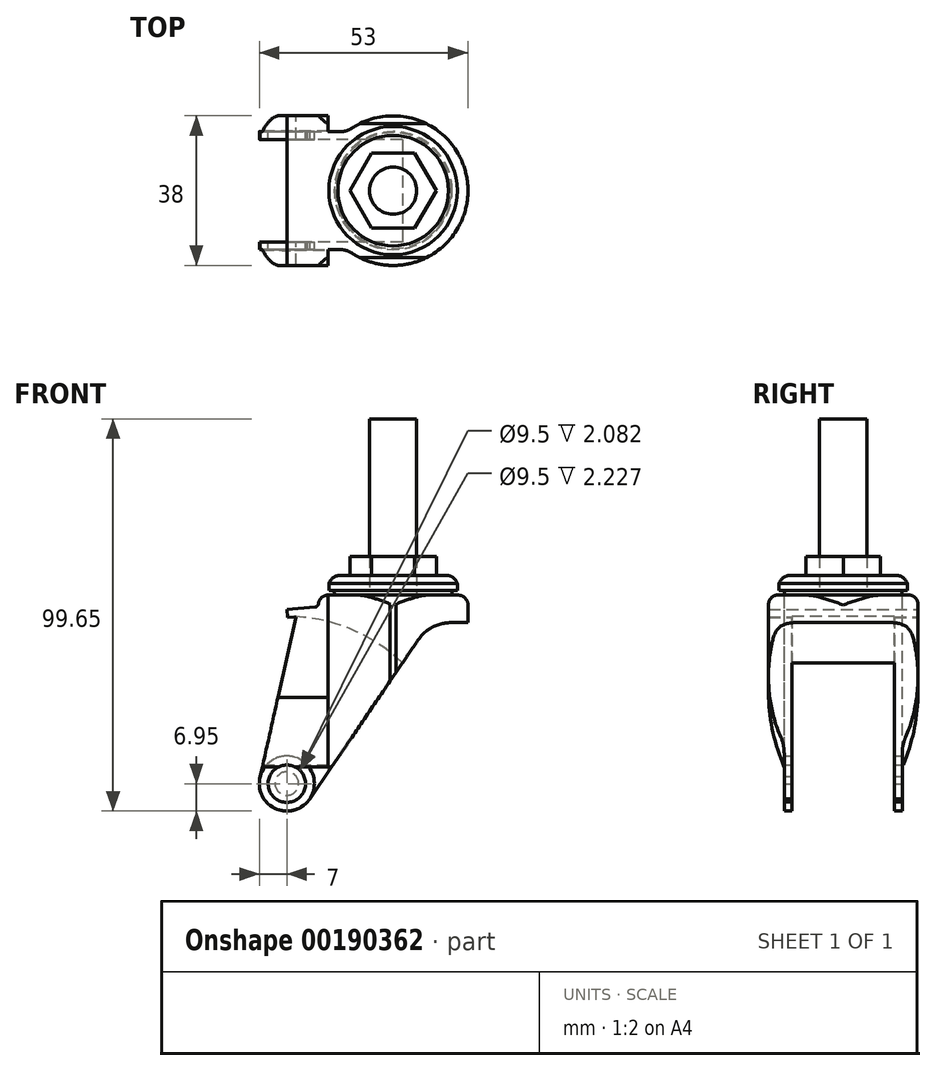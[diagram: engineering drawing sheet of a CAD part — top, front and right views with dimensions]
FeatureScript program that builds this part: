
annotation { "Feature Type Name" : "Feature", "Feature Type Description" : "" }
export const myFeature = defineFeature(function(context is Context, id is Id, definition is map)
    precondition{}
    {
        {
            var Q0;
            Q0=qCreatedBy(makeId("Top.planeOp"),FACE);
            var sketch = newSketch(context, id + "F0", { "sketchPlane" : qUnion([Q0])});
            skCircle(sketch, "E0", {"center": v(0, 0) * mm, "radius": 16.3 * mm});
            skArc(sketch, "E1", {"start": v(-10.5, -15.83) * mm, "mid": v(19, 0) * mm, "end": v(-10.5, 15.83) * mm});
            skLineSegment(sketch, "E2", {"start": v(22, 0) * mm, "end": v(-67.5, 0) * mm});
            skLineSegment(sketch, "E3", {"start": v(-31.35, 12.5) * mm, "end": v(-25.1, 12.5) * mm});
            skLineSegment(sketch, "E4", {"start": v(-25.25, 12) * mm, "end": v(-35, 12) * mm});
            skLineSegment(sketch, "E5", {"start": v(-31.35, -12.5) * mm, "end": v(-25.1, -12.5) * mm});
            skLineSegment(sketch, "E6", {"start": v(-25.25, -12) * mm, "end": v(-35, -12) * mm});
            skLineSegment(sketch, "E7", {"start": v(-25.67, -10.5) * mm, "end": v(-64.5, -10.5) * mm});
            skLineSegment(sketch, "E8", {"start": v(-25.67, 10.5) * mm, "end": v(-64.5, 10.5) * mm});
            skLineSegment(sketch, "E9", {"start": v(-30.25, -17.5) * mm, "end": v(-23.75, -17.5) * mm});
            skLineSegment(sketch, "E10", {"start": v(-29.75, 16.5) * mm, "end": v(-24.25, 16.5) * mm});
            skLineSegment(sketch, "E11", {"start": v(-24.94, 13) * mm, "end": v(-33.5, 13) * mm});
            skLineSegment(sketch, "E12", {"start": v(-13.27, 15) * mm, "end": v(-33.5, 15) * mm});
            skLineSegment(sketch, "E13", {"start": v(-24.94, -13) * mm, "end": v(-33.5, -13) * mm});
            skLineSegment(sketch, "E14", {"start": v(-13.27, -15) * mm, "end": v(-33.5, -15) * mm});
            skLineSegment(sketch, "E15", {"start": v(-30, -13) * mm, "end": v(-30, -12.5) * mm});
            skArc(sketch, "E16", {"start": v(-32.19, -12) * mm, "mid": v(-31.84, -12.37) * mm, "end": v(-31.35, -12.5) * mm});
            skLineSegment(sketch, "E17", {"start": v(-31.75, -16) * mm, "end": v(-31.75, -15.2) * mm});
            skArc(sketch, "E18", {"start": v(-31.55, -15) * mm, "mid": v(-31.7, -15.06) * mm, "end": v(-31.75, -15.2) * mm});
            skArc(sketch, "E19", {"start": v(-31.75, -16) * mm, "mid": v(-31.31, -17.06) * mm, "end": v(-30.25, -17.5) * mm});
            skLineSegment(sketch, "E20", {"start": v(-33.5, -13) * mm, "end": v(-33.5, -15) * mm});
            skLineSegment(sketch, "E21", {"start": v(-33.5, 15) * mm, "end": v(-33.5, 13) * mm});
            skArc(sketch, "E22", {"start": v(-31.35, 12.5) * mm, "mid": v(-31.84, 12.37) * mm, "end": v(-32.19, 12) * mm});
            skLineSegment(sketch, "E23", {"start": v(-30, 13) * mm, "end": v(-30, 12.5) * mm});
            skArc(sketch, "E24", {"start": v(-29.75, 16.5) * mm, "mid": v(-30.81, 16.06) * mm, "end": v(-31.25, 15) * mm});
            skLineSegment(sketch, "E25", {"start": v(-27, 19.5) * mm, "end": v(-27, -20.5) * mm});
            skLineSegment(sketch, "E26", {"start": v(5.48, -9.5) * mm, "end": v(10.97, 0) * mm});
            skLineSegment(sketch, "E27", {"start": v(-10.97, 0) * mm, "end": v(-5.48, -9.5) * mm});
            skCircle(sketch, "E28", {"center": v(0, 0) * mm, "radius": 6 * mm});
            skCircle(sketch, "E29", {"center": v(0, 0) * mm, "radius": 5.05 * mm});
            skCircle(sketch, "E30", {"center": v(0, 0) * mm, "radius": 4 * mm});
            skArc(sketch, "E31", {"start": v(-24.23, 15) * mm, "mid": v(-27, 0) * mm, "end": v(-24.23, -15) * mm});
            skArc(sketch, "E32", {"start": v(-13.86, 13) * mm, "mid": v(-19, 0) * mm, "end": v(-13.86, -13) * mm});
            skLineSegment(sketch, "E33", {"start": v(0, -22) * mm, "end": v(0, 22) * mm});
            skLineSegment(sketch, "E34", {"start": v(-22.25, -16) * mm, "end": v(-22.25, -15.2) * mm});
            skArc(sketch, "E35", {"start": v(-22.25, -15.2) * mm, "mid": v(-22.3, -15.06) * mm, "end": v(-22.45, -15) * mm});
            skArc(sketch, "E36", {"start": v(-23.75, -17.5) * mm, "mid": v(-22.69, -17.06) * mm, "end": v(-22.25, -16) * mm});
            skArc(sketch, "E37", {"start": v(-10.5, -15.83) * mm, "mid": v(-11.82, -15.21) * mm, "end": v(-13.27, -15) * mm});
            skLineSegment(sketch, "E38", {"start": v(-5.48, -9.5) * mm, "end": v(5.48, -9.5) * mm});
            skLineSegment(sketch, "E39", {"start": v(-5.48, 9.5) * mm, "end": v(-10.97, 0) * mm});
            skArc(sketch, "E40", {"start": v(-22.75, 15) * mm, "mid": v(-23.19, 16.06) * mm, "end": v(-24.25, 16.5) * mm});
            skArc(sketch, "E41", {"start": v(-13.27, 15) * mm, "mid": v(-11.82, 15.21) * mm, "end": v(-10.5, 15.83) * mm});
            skLineSegment(sketch, "E42", {"start": v(5.48, 9.5) * mm, "end": v(-5.48, 9.5) * mm});
            skLineSegment(sketch, "E43", {"start": v(10.97, 0) * mm, "end": v(5.48, 9.5) * mm});
            skLineSegment(sketch, "E44", {"start": v(-64.5, 10.5) * mm, "end": v(-64.5, -10.5) * mm});
            skLineSegment(sketch, "E45", {"start": v(-35, -12) * mm, "end": v(-35, -10.5) * mm});
            skLineSegment(sketch, "E46", {"start": v(-35, 10.5) * mm, "end": v(-35, 12) * mm});
            skSolve(sketch);
        }
        {
            var Q0;
            Q0=qCreatedBy(makeId("Front.planeOp"),FACE);
            var sketch = newSketch(context, id + "F1", { "sketchPlane" : qUnion([Q0])});
            skArc(sketch, "E47", {"start": v(10.72, -7.97) * mm, "mid": v(11.8, -7.76) * mm, "end": v(12.75, -7.18) * mm});
            skLineSegment(sketch, "E48", {"start": v(-67.5, -47.93) * mm, "end": v(13.5, -47.93) * mm});
            skArc(sketch, "E49", {"start": v(14.63, -7) * mm, "mid": v(9.95, -8.16) * mm, "end": v(6.36, -11.37) * mm});
            skLineSegment(sketch, "E50", {"start": v(-12.46, -6.65) * mm, "end": v(-12.46, -34.22) * mm});
            skLineSegment(sketch, "E51", {"start": v(-24.23, -3.46) * mm, "end": v(-33.83, -46.4) * mm});
            skLineSegment(sketch, "E52", {"start": v(0, 47.77) * mm, "end": v(0, -26.76) * mm});
            skArc(sketch, "E53", {"start": v(-25.8, -10.45) * mm, "mid": v(-41.9, -82.34) * mm, "end": v(-0.48, -21.42) * mm});
            skLineSegment(sketch, "E54", {"start": v(-27, -88.43) * mm, "end": v(-27, -40.18) * mm});
            skArc(sketch, "E55", {"start": v(-33.8, -46.3) * mm, "mid": v(-29.83, -54.33) * mm, "end": v(-21.21, -51.87) * mm});
            skCircle(sketch, "E56", {"center": v(-27, -47.93) * mm, "radius": 4.75 * mm});
            skLineSegment(sketch, "E57", {"start": v(6.36, -11.37) * mm, "end": v(-21.21, -51.87) * mm});
            skLineSegment(sketch, "E58", {"start": v(6, 10.37) * mm, "end": v(6, 42.77) * mm});
            skLineSegment(sketch, "E59", {"start": v(5.05, 12.01) * mm, "end": v(5.05, 43.72) * mm});
            skLineSegment(sketch, "E60", {"start": v(-6, 10.37) * mm, "end": v(-6, 42.77) * mm});
            skLineSegment(sketch, "E61", {"start": v(-5.05, 12.01) * mm, "end": v(-5.05, 43.72) * mm});
            skLineSegment(sketch, "E62", {"start": v(-14.05, 4.97) * mm, "end": v(14.05, 4.97) * mm});
            skLineSegment(sketch, "E63", {"start": v(16.3, 2.97) * mm, "end": v(-16.3, 2.97) * mm});
            skLineSegment(sketch, "E64", {"start": v(10.97, 9.77) * mm, "end": v(-10.97, 9.77) * mm});
            skLineSegment(sketch, "E65", {"start": v(16.3, 1.17) * mm, "end": v(-16.3, 1.17) * mm});
            skLineSegment(sketch, "E66", {"start": v(-16.51, 0) * mm, "end": v(16.5, 0) * mm});
            skLineSegment(sketch, "E67", {"start": v(-10.97, 9.77) * mm, "end": v(-10.97, 5.32) * mm});
            skLineSegment(sketch, "E68", {"start": v(-13.37, -2.5) * mm, "end": v(-27, -3.7) * mm});
            skArc(sketch, "E69", {"start": v(-16.5, 0) * mm, "mid": v(-18.16, -0.63) * mm, "end": v(-18.98, -2.2) * mm});
            skLineSegment(sketch, "E70", {"start": v(-27, -3.7) * mm, "end": v(-26.83, -5.7) * mm});
            skLineSegment(sketch, "E71", {"start": v(-24.69, -5.5) * mm, "end": v(-26.83, -5.7) * mm});
            skArc(sketch, "E72", {"start": v(-19.89, -3.08) * mm, "mid": v(-19.28, -2.8) * mm, "end": v(-18.98, -2.2) * mm});
            skArc(sketch, "E73", {"start": v(-10.9, 5.27) * mm, "mid": v(-10.6, 5.11) * mm, "end": v(-10.3, 4.97) * mm});
            skLineSegment(sketch, "E74", {"start": v(-10.37, 4.97) * mm, "end": v(-10.97, 5.32) * mm});
            skArc(sketch, "E75", {"start": v(-14.05, 4.97) * mm, "mid": v(-15.44, 4.27) * mm, "end": v(-16.3, 2.97) * mm});
            skArc(sketch, "E76", {"start": v(-14.98, 1.17) * mm, "mid": v(-14.94, 0.57) * mm, "end": v(-14.72, 0) * mm});
            skLineSegment(sketch, "E77", {"start": v(-13, 2.57) * mm, "end": v(-13, -1.5) * mm});
            skLineSegment(sketch, "E78", {"start": v(-16.3, 2.97) * mm, "end": v(-16.3, 1.17) * mm});
            skLineSegment(sketch, "E79", {"start": v(10.97, 9.77) * mm, "end": v(10.97, 5.32) * mm});
            skLineSegment(sketch, "E80", {"start": v(-5.48, 9.77) * mm, "end": v(-5.48, 5.32) * mm});
            skLineSegment(sketch, "E81", {"start": v(10.72, -7.97) * mm, "end": v(10.33, -7.97) * mm});
            skArc(sketch, "E82", {"start": v(-5.48, 5.32) * mm, "mid": v(-4.86, 5.13) * mm, "end": v(-4.23, 4.97) * mm});
            skArc(sketch, "E83", {"start": v(-6, 4.97) * mm, "mid": v(-5.73, 5.13) * mm, "end": v(-5.48, 5.32) * mm});
            skLineSegment(sketch, "E84", {"start": v(-6, 12.01) * mm, "end": v(6, 12.01) * mm});
            skArc(sketch, "E85", {"start": v(-6.6, 9.77) * mm, "mid": v(-6.18, 9.95) * mm, "end": v(-6, 10.37) * mm});
            skLineSegment(sketch, "E86", {"start": v(-5.05, 12.01) * mm, "end": v(-6, 10.37) * mm});
            skLineSegment(sketch, "E87", {"start": v(5.05, 12.01) * mm, "end": v(6, 10.37) * mm});
            skArc(sketch, "E88", {"start": v(6, 10.37) * mm, "mid": v(6.18, 9.95) * mm, "end": v(6.6, 9.77) * mm});
            skLineSegment(sketch, "E89", {"start": v(4, 44.77) * mm, "end": v(-4, 44.77) * mm});
            skLineSegment(sketch, "E90", {"start": v(6, 42.77) * mm, "end": v(-6, 42.77) * mm});
            skLineSegment(sketch, "E91", {"start": v(-4, 44.77) * mm, "end": v(-6, 42.77) * mm});
            skLineSegment(sketch, "E92", {"start": v(6, 42.77) * mm, "end": v(4, 44.77) * mm});
            skLineSegment(sketch, "E93", {"start": v(19, -2.5) * mm, "end": v(19, -6) * mm});
            skLineSegment(sketch, "E94", {"start": v(19, -2.9) * mm, "end": v(19, -7) * mm});
            skLineSegment(sketch, "E95", {"start": v(14.63, -7) * mm, "end": v(19, -7) * mm});
            skArc(sketch, "E96", {"start": v(16.3, 2.97) * mm, "mid": v(15.44, 4.27) * mm, "end": v(14.05, 4.97) * mm});
            skLineSegment(sketch, "E97", {"start": v(16.3, 2.97) * mm, "end": v(16.3, 1.17) * mm});
            skArc(sketch, "E98", {"start": v(19, -2.5) * mm, "mid": v(18.27, -0.73) * mm, "end": v(16.5, 0) * mm});
            skLineSegment(sketch, "E99", {"start": v(10.37, 4.97) * mm, "end": v(10.97, 5.32) * mm});
            skArc(sketch, "E100", {"start": v(10.3, 4.97) * mm, "mid": v(10.6, 5.11) * mm, "end": v(10.9, 5.27) * mm});
            skArc(sketch, "E101", {"start": v(5.48, 5.32) * mm, "mid": v(5.73, 5.13) * mm, "end": v(6, 4.97) * mm});
            skArc(sketch, "E102", {"start": v(4.23, 4.97) * mm, "mid": v(4.86, 5.13) * mm, "end": v(5.48, 5.32) * mm});
            skLineSegment(sketch, "E103", {"start": v(13, 2.57) * mm, "end": v(13, -1.5) * mm});
            skArc(sketch, "E104", {"start": v(14.72, 0) * mm, "mid": v(14.94, 0.57) * mm, "end": v(14.98, 1.17) * mm});
            skLineSegment(sketch, "E105", {"start": v(5.48, 9.77) * mm, "end": v(5.48, 5.32) * mm});
            skSolve(sketch);
        }
        {
            var Q0;
            Q0=qCreatedBy(makeId("Right.planeOp"),FACE);
            var sketch = newSketch(context, id + "F2", { "sketchPlane" : qUnion([Q0])});
            skLineSegment(sketch, "E106", {"start": v(13.01, -54.88) * mm, "end": v(13.01, -6.64) * mm});
            skLineSegment(sketch, "E107", {"start": v(15.01, -54.88) * mm, "end": v(15.01, -6.65) * mm});
            skLineSegment(sketch, "E108", {"start": v(19.01, -25.96) * mm, "end": v(19.01, -2.45) * mm});
            skLineSegment(sketch, "E109", {"start": v(-18.99, -25.96) * mm, "end": v(-18.99, -2.45) * mm});
            skLineSegment(sketch, "E110", {"start": v(-14.99, -54.88) * mm, "end": v(-14.99, -6.65) * mm});
            skLineSegment(sketch, "E111", {"start": v(-12.99, -54.88) * mm, "end": v(-12.99, -6.64) * mm});
            skLineSegment(sketch, "E112", {"start": v(0.01, 47.77) * mm, "end": v(0.01, -88.38) * mm});
            skArc(sketch, "E113", {"start": v(-18.99, -25.96) * mm, "mid": v(-17.81, -34.98) * mm, "end": v(-15.04, -43.63) * mm});
            skLineSegment(sketch, "E114", {"start": v(20.26, -47.88) * mm, "end": v(-19.24, -47.88) * mm});
            skLineSegment(sketch, "E115", {"start": v(12.01, -55.88) * mm, "end": v(12.01, -39.88) * mm});
            skLineSegment(sketch, "E116", {"start": v(10.51, -85.38) * mm, "end": v(10.51, -10.38) * mm});
            skLineSegment(sketch, "E117", {"start": v(-11.99, -55.88) * mm, "end": v(-11.99, -39.88) * mm});
            skLineSegment(sketch, "E118", {"start": v(-10.49, -85.38) * mm, "end": v(-10.49, -10.38) * mm});
            skArc(sketch, "E119", {"start": v(15.28, -43.13) * mm, "mid": v(17.9, -34.71) * mm, "end": v(19.01, -25.96) * mm});
            skLineSegment(sketch, "E120", {"start": v(-12.99, -44.88) * mm, "end": v(-11.99, -44.88) * mm});
            skLineSegment(sketch, "E121", {"start": v(-14.99, -54.88) * mm, "end": v(-12.99, -54.88) * mm});
            skArc(sketch, "E122", {"start": v(-14.99, -43.63) * mm, "mid": v(-16.05, -44.07) * mm, "end": v(-16.49, -45.13) * mm});
            skArc(sketch, "E123", {"start": v(-16.49, -50.63) * mm, "mid": v(-16.05, -51.7) * mm, "end": v(-14.99, -52.13) * mm});
            skLineSegment(sketch, "E124", {"start": v(-16.49, -50.63) * mm, "end": v(-16.49, -45.13) * mm});
            skLineSegment(sketch, "E125", {"start": v(13.01, -44.88) * mm, "end": v(12.01, -44.88) * mm});
            skLineSegment(sketch, "E126", {"start": v(13.01, -54.88) * mm, "end": v(15.01, -54.88) * mm});
            skArc(sketch, "E127", {"start": v(17.51, -44.63) * mm, "mid": v(17.08, -43.57) * mm, "end": v(16.01, -43.13) * mm});
            skArc(sketch, "E128", {"start": v(15.22, -43.13) * mm, "mid": v(15.08, -43.19) * mm, "end": v(15.01, -43.33) * mm});
            skLineSegment(sketch, "E129", {"start": v(16.01, -43.13) * mm, "end": v(15.21, -43.13) * mm});
            skArc(sketch, "E130", {"start": v(16.01, -52.63) * mm, "mid": v(17.08, -52.2) * mm, "end": v(17.51, -51.13) * mm});
            skArc(sketch, "E131", {"start": v(15.01, -52.43) * mm, "mid": v(15.08, -52.57) * mm, "end": v(15.22, -52.63) * mm});
            skLineSegment(sketch, "E132", {"start": v(16.01, -52.63) * mm, "end": v(15.21, -52.63) * mm});
            skLineSegment(sketch, "E133", {"start": v(17.51, -51.13) * mm, "end": v(17.51, -44.63) * mm});
            skArc(sketch, "E134", {"start": v(-16.49, 0.05) * mm, "mid": v(-18.25, -0.68) * mm, "end": v(-18.99, -2.45) * mm});
            skLineSegment(sketch, "E135", {"start": v(5.07, 12.01) * mm, "end": v(5.07, 43.72) * mm});
            skLineSegment(sketch, "E136", {"start": v(6.01, 10.37) * mm, "end": v(6.01, 42.77) * mm});
            skLineSegment(sketch, "E137", {"start": v(-5.04, 12.01) * mm, "end": v(-5.04, 43.72) * mm});
            skLineSegment(sketch, "E138", {"start": v(-5.99, 10.37) * mm, "end": v(-5.99, 42.77) * mm});
            skLineSegment(sketch, "E139", {"start": v(10.73, -7.92) * mm, "end": v(-10.7, -7.92) * mm});
            skLineSegment(sketch, "E140", {"start": v(-14.04, 4.97) * mm, "end": v(14.06, 4.97) * mm});
            skLineSegment(sketch, "E141", {"start": v(9.51, 5.32) * mm, "end": v(-9.49, 5.32) * mm});
            skLineSegment(sketch, "E142", {"start": v(-9.49, 9.77) * mm, "end": v(9.51, 9.77) * mm});
            skLineSegment(sketch, "E143", {"start": v(-5.99, 12.01) * mm, "end": v(6.01, 12.01) * mm});
            skLineSegment(sketch, "E144", {"start": v(16.31, 1.17) * mm, "end": v(-16.29, 1.17) * mm});
            skLineSegment(sketch, "E145", {"start": v(16.31, 2.97) * mm, "end": v(-16.29, 2.97) * mm});
            skLineSegment(sketch, "E146", {"start": v(-11.99, -5.64) * mm, "end": v(12.01, -5.64) * mm});
            skLineSegment(sketch, "E147", {"start": v(-11.99, -3.65) * mm, "end": v(12.01, -3.65) * mm});
            skLineSegment(sketch, "E148", {"start": v(-16.5, 0.05) * mm, "end": v(16.51, 0.05) * mm});
            skLineSegment(sketch, "E149", {"start": v(0.01, 9.77) * mm, "end": v(0.01, 5.32) * mm});
            skLineSegment(sketch, "E150", {"start": v(-9.49, 5.32) * mm, "end": v(-9.49, 9.77) * mm});
            skLineSegment(sketch, "E151", {"start": v(-8.88, 4.97) * mm, "end": v(-9.49, 5.32) * mm});
            skArc(sketch, "E152", {"start": v(-9.49, 5.32) * mm, "mid": v(-8.95, 5.14) * mm, "end": v(-8.4, 4.97) * mm});
            skArc(sketch, "E153", {"start": v(-12.99, -6.87) * mm, "mid": v(-11.96, -7.64) * mm, "end": v(-10.7, -7.92) * mm});
            skArc(sketch, "E154", {"start": v(-14.04, 4.97) * mm, "mid": v(-15.43, 4.28) * mm, "end": v(-16.29, 2.97) * mm});
            skLineSegment(sketch, "E155", {"start": v(-12.99, 2.62) * mm, "end": v(-12.99, -1.45) * mm});
            skArc(sketch, "E156", {"start": v(-14.96, 1.17) * mm, "mid": v(-14.93, 0.57) * mm, "end": v(-14.7, 0) * mm});
            skLineSegment(sketch, "E157", {"start": v(-16.29, 2.97) * mm, "end": v(-16.29, 1.17) * mm});
            skArc(sketch, "E158", {"start": v(-11.99, -3.65) * mm, "mid": v(-14.1, -4.52) * mm, "end": v(-14.99, -6.65) * mm});
            skArc(sketch, "E159", {"start": v(-11.99, -5.64) * mm, "mid": v(-12.7, -5.93) * mm, "end": v(-12.99, -6.64) * mm});
            skArc(sketch, "E160", {"start": v(0.01, 5.32) * mm, "mid": v(0.55, 5.14) * mm, "end": v(1.1, 4.97) * mm});
            skArc(sketch, "E161", {"start": v(-1.07, 4.97) * mm, "mid": v(-0.52, 5.14) * mm, "end": v(0.01, 5.32) * mm});
            skLineSegment(sketch, "E162", {"start": v(-5.04, 12.01) * mm, "end": v(-5.99, 10.37) * mm});
            skArc(sketch, "E163", {"start": v(-6.59, 9.77) * mm, "mid": v(-6.16, 9.95) * mm, "end": v(-5.99, 10.37) * mm});
            skLineSegment(sketch, "E164", {"start": v(9.51, 5.32) * mm, "end": v(9.51, 9.77) * mm});
            skArc(sketch, "E165", {"start": v(10.73, -7.92) * mm, "mid": v(11.99, -7.64) * mm, "end": v(13.01, -6.87) * mm});
            skLineSegment(sketch, "E166", {"start": v(8.91, 4.97) * mm, "end": v(9.51, 5.32) * mm});
            skArc(sketch, "E167", {"start": v(8.43, 4.97) * mm, "mid": v(8.98, 5.14) * mm, "end": v(9.51, 5.32) * mm});
            skLineSegment(sketch, "E168", {"start": v(16.31, 2.97) * mm, "end": v(16.31, 1.17) * mm});
            skLineSegment(sketch, "E169", {"start": v(13.01, 2.62) * mm, "end": v(13.01, -1.45) * mm});
            skArc(sketch, "E170", {"start": v(14.74, 0) * mm, "mid": v(14.95, 0.57) * mm, "end": v(15, 1.17) * mm});
            skArc(sketch, "E171", {"start": v(16.31, 2.97) * mm, "mid": v(15.46, 4.28) * mm, "end": v(14.06, 4.97) * mm});
            skArc(sketch, "E172", {"start": v(19.01, -2.45) * mm, "mid": v(18.28, -0.68) * mm, "end": v(16.51, 0.05) * mm});
            skArc(sketch, "E173", {"start": v(13.01, -6.64) * mm, "mid": v(12.72, -5.93) * mm, "end": v(12.01, -5.64) * mm});
            skArc(sketch, "E174", {"start": v(15.01, -6.65) * mm, "mid": v(14.14, -4.52) * mm, "end": v(12.01, -3.65) * mm});
            skLineSegment(sketch, "E175", {"start": v(5.07, 12.01) * mm, "end": v(6.01, 10.37) * mm});
            skArc(sketch, "E176", {"start": v(6.01, 10.37) * mm, "mid": v(6.2, 9.95) * mm, "end": v(6.61, 9.77) * mm});
            skLineSegment(sketch, "E177", {"start": v(4.01, 44.77) * mm, "end": v(-3.99, 44.77) * mm});
            skLineSegment(sketch, "E178", {"start": v(6.01, 42.77) * mm, "end": v(-5.99, 42.77) * mm});
            skLineSegment(sketch, "E179", {"start": v(-3.99, 44.77) * mm, "end": v(-5.99, 42.77) * mm});
            skLineSegment(sketch, "E180", {"start": v(6.01, 42.77) * mm, "end": v(4.01, 44.77) * mm});
            skLineSegment(sketch, "E181", {"start": v(12.01, -39.88) * mm, "end": v(10.51, -39.88) * mm});
            skLineSegment(sketch, "E182", {"start": v(-10.49, -10.38) * mm, "end": v(10.51, -10.38) * mm});
            skLineSegment(sketch, "E183", {"start": v(-10.49, -39.88) * mm, "end": v(-11.99, -39.88) * mm});
            skLineSegment(sketch, "E184", {"start": v(-10.49, -85.38) * mm, "end": v(10.51, -85.38) * mm});
            skLineSegment(sketch, "E185", {"start": v(-10.49, -55.88) * mm, "end": v(-11.99, -55.88) * mm});
            skLineSegment(sketch, "E186", {"start": v(12.01, -55.88) * mm, "end": v(10.51, -55.88) * mm});
            skLineSegment(sketch, "E187", {"start": v(-12.99, -50.88) * mm, "end": v(-11.99, -50.88) * mm});
            skLineSegment(sketch, "E188", {"start": v(13.01, -50.88) * mm, "end": v(12.01, -50.88) * mm});
            skSolve(sketch);
        }
        {
            var Q0;
            Q0=qCreatedBy(makeId("Front.planeOp"),FACE);
            var sketch = newSketch(context, id + "F3", { "sketchPlane" : qUnion([Q0])});
            skLineSegment(sketch, "E189", {"start": v(0, 60.42) * mm, "end": v(0, -88.2) * mm, "construction": true});
            skLineSegment(sketch, "E190", {"start": v(-75.21, 0) * mm, "end": v(74.5, 0) * mm, "construction": true});
            skLineSegment(sketch, "E191.0", {"start": v(-67.5, -47.93) * mm, "end": v(13.5, -47.93) * mm, "construction": true});
            skLineSegment(sketch, "E192.0", {"start": v(-27, -88.43) * mm, "end": v(-27, -40.18) * mm, "construction": true});
            skArc(sketch, "E193.0", {"start": v(-25.8, -10.45) * mm, "mid": v(-41.9, -82.34) * mm, "end": v(-0.48, -21.42) * mm, "construction": true});
            skCircle(sketch, "E194", {"center": v(-27, -47.93) * mm, "radius": 37.5 * mm});
            skSolve(sketch);
        }
        {
            var Q0;
            Q0 = qSketchRegion(id + "F3", true);
            extrude(context, id + "F4", {"entities" : qUnion([Q0]), "endBound" : BoundingType.SYMMETRIC, "depth" : 21 * mm});
        }
        {
            var Q0;
            Q0=qCreatedBy(makeId("Top.planeOp"),FACE);
            var sketch = newSketch(context, id + "F5", { "sketchPlane" : qUnion([Q0])});
            skCircle(sketch, "E195.0", {"center": v(0, 0) * mm, "radius": 6 * mm});
            skSolve(sketch);
        }
        {
            var Q0;
            Q0 = qSketchRegion(id + "F5", true);
            extrude(context, id + "F6", {"entities" : qUnion([Q0]), "depth" : 44.77 * mm});
        }
        {
            var Q0;
            Q0=sQuery(id+"F1.wireOp",EDGE,"E54");
            var Q1;
            Q1=qCreatedBy(makeId("Right.planeOp"),FACE);
            cPlane(context, id + "F7", {"entities" : qUnion([Q0, Q1]), "cplaneType" : CPlaneType.LINE_ANGLE, "offset" : 25 * mm, "angle" : 0 * degree, "width" : 150 * mm, "height" : 150 * mm});
        }
        {
            var Q0;
            Q0=qCreatedBy(id+"F7.planeOp",FACE);
            var sketch = newSketch(context, id + "F8", { "sketchPlane" : qUnion([Q0])});
            skLineSegment(sketch, "E196.0", {"start": v(-20.26, -47.88) * mm, "end": v(19.24, -47.88) * mm, "construction": true});
            skLineSegment(sketch, "E197.0", {"start": v(16.49, -50.63) * mm, "end": v(16.49, -47.88) * mm});
            skArc(sketch, "E198.0", {"start": v(16.49, -50.63) * mm, "mid": v(16.05, -51.7) * mm, "end": v(14.99, -52.13) * mm});
            skLineSegment(sketch, "E199.0", {"start": v(14.99, -54.88) * mm, "end": v(14.99, -47.88) * mm});
            skLineSegment(sketch, "E200.0", {"start": v(14.99, -54.88) * mm, "end": v(12.99, -54.88) * mm});
            skLineSegment(sketch, "E201.0", {"start": v(12.99, -54.88) * mm, "end": v(12.99, -47.88) * mm});
            skPoint(sketch, "E202.0", {"position": v(12.49, -50.88) * mm});
            skLineSegment(sketch, "E203.0", {"start": v(11.99, -55.88) * mm, "end": v(11.99, -47.88) * mm});
            skLineSegment(sketch, "E204.0", {"start": v(12.99, -50.88) * mm, "end": v(11.99, -50.88) * mm});
            skPoint(sketch, "E205.0", {"position": v(11.24, -55.88) * mm});
            skLineSegment(sketch, "E206.0", {"start": v(10.49, -55.88) * mm, "end": v(11.99, -55.88) * mm});
            skLineSegment(sketch, "E207.0", {"start": v(-12.01, -55.88) * mm, "end": v(-10.51, -55.88) * mm});
            skLineSegment(sketch, "E208.0", {"start": v(-12.01, -55.88) * mm, "end": v(-12.01, -47.88) * mm});
            skLineSegment(sketch, "E209.0", {"start": v(-13.01, -50.88) * mm, "end": v(-12.01, -50.88) * mm});
            skLineSegment(sketch, "E210.0", {"start": v(-13.01, -54.88) * mm, "end": v(-13.01, -47.88) * mm});
            skLineSegment(sketch, "E211.0", {"start": v(-13.01, -54.88) * mm, "end": v(-15.01, -54.88) * mm});
            skLineSegment(sketch, "E212.0", {"start": v(-15.01, -54.88) * mm, "end": v(-15.01, -47.88) * mm});
            skArc(sketch, "E213.0", {"start": v(-15.01, -52.43) * mm, "mid": v(-15.08, -52.57) * mm, "end": v(-15.22, -52.63) * mm});
            skLineSegment(sketch, "E214.0", {"start": v(-16.01, -52.63) * mm, "end": v(-15.21, -52.63) * mm});
            skArc(sketch, "E215.0", {"start": v(-16.01, -52.63) * mm, "mid": v(-17.08, -52.2) * mm, "end": v(-17.51, -51.13) * mm});
            skLineSegment(sketch, "E216.0", {"start": v(-17.51, -51.13) * mm, "end": v(-17.51, -47.88) * mm});
            skPoint(sketch, "E217.orphan", {"position": v(14.99, -6.65) * mm});
            skPoint(sketch, "E218.orphan", {"position": v(12.99, -6.64) * mm});
            skPoint(sketch, "E219.orphan", {"position": v(-13.01, -6.64) * mm});
            skPoint(sketch, "E220.orphan", {"position": v(-15.01, -6.65) * mm});
            skLineSegment(sketch, "E221", {"start": v(-17.51, -47.88) * mm, "end": v(16.49, -47.88) * mm});
            skLineSegment(sketch, "E222", {"start": v(-10.51, -55.88) * mm, "end": v(10.49, -55.88) * mm});
            skSolve(sketch);
        }
        {
            var Q0;
            {var subQ5=sQuery(id+"F8.wireOp",EDGE,"E206.0");Q0=makeQuery(id+"F8.imprint","IMPRINT",FACE,{"disambiguationData":[TD([[makeQuery(id+"F8.imprint","IMPRINT",EDGE,{"derivedFrom":subQ5}),1.0]])]});}
            var Q1;
            Q1=sQuery(id+"F8.wireOp",EDGE,"E221");
            revolve(context, id + "F9", {"entities" : qUnion([Q0]), "axis" : qUnion([Q1]), "revolveType" : RevolveType.FULL});
        }
        {
            var Q0;
            {var subQ3=sQuery(id+"F8.wireOp",EDGE,"E204.0");Q0=makeQuery(id+"F8.imprint","IMPRINT",FACE,{"disambiguationData":[TD([[makeQuery(id+"F8.imprint","IMPRINT",EDGE,{"derivedFrom":subQ3}),-1.0]])]});}
            var Q1;
            {var subQ3=sQuery(id+"F8.wireOp",EDGE,"E209.0");Q1=makeQuery(id+"F8.imprint","IMPRINT",FACE,{"disambiguationData":[TD([[makeQuery(id+"F8.imprint","IMPRINT",EDGE,{"derivedFrom":subQ3}),1.0]])]});}
            var Q2;
            Q2=sQuery(id+"F8.wireOp",EDGE,"E221");
            revolve(context, id + "F10", {"entities" : qUnion([Q0, Q1]), "axis" : qUnion([Q2]), "revolveType" : RevolveType.FULL});
        }
        {
            var Q0;
            {var subQ1=sQuery(id+"F8.wireOp",EDGE,"E200.0");Q0=makeQuery(id+"F8.imprint","IMPRINT",FACE,{"disambiguationData":[TD([[makeQuery(id+"F8.imprint","IMPRINT",EDGE,{"derivedFrom":subQ1}),-1.0]])]});}
            var Q1;
            {var subQ0=sQuery(id+"F8.wireOp",EDGE,"E211.0");Q1=makeQuery(id+"F8.imprint","IMPRINT",FACE,{"disambiguationData":[TD([[makeQuery(id+"F8.imprint","IMPRINT",EDGE,{"derivedFrom":subQ0}),-1.0]])]});}
            var Q2;
            Q2=sQuery(id+"F8.wireOp",EDGE,"E221");
            revolve(context, id + "F11", {"entities" : qUnion([Q0, Q1]), "axis" : qUnion([Q2]), "revolveType" : RevolveType.FULL});
        }
        {
            var Q0;
            {var subQ0=sQuery(id+"F8.wireOp",EDGE,"E197.0");Q0=makeQuery(id+"F8.imprint","IMPRINT",FACE,{"disambiguationData":[TD([[makeQuery(id+"F8.imprint","IMPRINT",EDGE,{"derivedFrom":subQ0}),1.0]])]});}
            var Q1;
            {var subQ0=sQuery(id+"F8.wireOp",EDGE,"E214.0");Q1=makeQuery(id+"F8.imprint","IMPRINT",FACE,{"disambiguationData":[TD([[makeQuery(id+"F8.imprint","IMPRINT",EDGE,{"derivedFrom":subQ0}),1.0]])]});}
            var Q2;
            Q2=sQuery(id+"F8.wireOp",EDGE,"E221");
            revolve(context, id + "F12", {"entities" : qUnion([Q0, Q1]), "axis" : qUnion([Q2]), "revolveType" : RevolveType.FULL});
        }
        {
            var Q0;
            Q0=makeQuery(id+"F4.opExtrude","CAP_EDGE",EDGE,{"disambiguationData":[OSD([sQuery(id+"F3.wireOp",EDGE,"E194")])],"isStart":false});
            var Q1;
            Q1=makeQuery(id+"F4.opExtrude","CAP_EDGE",EDGE,{"disambiguationData":[OSD([sQuery(id+"F3.wireOp",EDGE,"E194")])],"isStart":true});
            fillet(context, id + "F13", {"entities" : qUnion([Q0, Q1]), "radius" : 2 * mm, "tangentPropagation" : true, "allowEdgeOverflow" : false});
        }
        {
            var Q0;
            Q0=qCreatedBy(makeId("Front.planeOp"),FACE);
            var sketch = newSketch(context, id + "F14", { "sketchPlane" : qUnion([Q0])});
            skLineSegment(sketch, "E223.0", {"start": v(0, 47.77) * mm, "end": v(0, -88.38) * mm});
            skLineSegment(sketch, "E224.0", {"start": v(0, 4.97) * mm, "end": v(14.05, 4.97) * mm});
            skArc(sketch, "E225.0", {"start": v(16.3, 2.97) * mm, "mid": v(15.44, 4.27) * mm, "end": v(14.05, 4.97) * mm});
            skLineSegment(sketch, "E226.0", {"start": v(16.3, 2.97) * mm, "end": v(16.3, 1.17) * mm});
            skLineSegment(sketch, "E227.0", {"start": v(16.3, 2.97) * mm, "end": v(0, 2.97) * mm});
            skLineSegment(sketch, "E228.0", {"start": v(16.3, 1.17) * mm, "end": v(0, 1.17) * mm});
            skArc(sketch, "E229.0", {"start": v(14.72, 0) * mm, "mid": v(14.94, 0.57) * mm, "end": v(14.98, 1.17) * mm});
            skLineSegment(sketch, "E230.0", {"start": v(0, 0) * mm, "end": v(16.5, 0) * mm});
            skPoint(sketch, "E231.orphan", {"position": v(-14.05, 4.97) * mm});
            skPoint(sketch, "E232.orphan", {"position": v(-16.3, 2.97) * mm});
            skPoint(sketch, "E233.orphan", {"position": v(-16.3, 1.17) * mm});
            skPoint(sketch, "E234.orphan", {"position": v(-16.51, 0) * mm});
            skSolve(sketch);
        }
        {
            var Q0;
            Q0 = qSketchRegion(id + "F14", true);
            var Q1;
            Q1=sQuery(id+"F14.wireOp",EDGE,"E223.0");
            revolve(context, id + "F15", {"entities" : qUnion([Q0]), "axis" : qUnion([Q1]), "revolveType" : RevolveType.FULL});
        }
        {
            var Q0;
            Q0=makeQuery(id+"F15.opRevolve","SWEPT_FACE",FACE,{"disambiguationData":[OSD([sQuery(id+"F14.wireOp",EDGE,"E224.0")])]});
            var sketch = newSketch(context, id + "F16", { "sketchPlane" : qUnion([Q0])});
            skLineSegment(sketch, "E235.0", {"start": v(-5.48, 9.5) * mm, "end": v(-10.97, 0) * mm});
            skLineSegment(sketch, "E236.0", {"start": v(5.48, 9.5) * mm, "end": v(-5.48, 9.5) * mm});
            skLineSegment(sketch, "E237.0", {"start": v(10.97, 0) * mm, "end": v(5.48, 9.5) * mm});
            skLineSegment(sketch, "E238.0", {"start": v(5.48, -9.5) * mm, "end": v(10.97, 0) * mm});
            skLineSegment(sketch, "E239.0", {"start": v(-5.48, -9.5) * mm, "end": v(5.48, -9.5) * mm});
            skLineSegment(sketch, "E240.0", {"start": v(-10.97, 0) * mm, "end": v(-5.48, -9.5) * mm});
            skLineSegment(sketch, "E241.0", {"start": v(10.97, 0) * mm, "end": v(-10.97, 0) * mm});
            skSolve(sketch);
        }
        {
            var Q0;
            Q0 = qSketchRegion(id + "F16", true);
            extrude(context, id + "F17", {"entities" : qUnion([Q0]), "depth" : 4.9 * mm});
        }
        {
            var Q0;
            Q0=qCreatedBy(makeId("Front.planeOp"),FACE);
            var sketch = newSketch(context, id + "F18", { "sketchPlane" : qUnion([Q0])});
            skArc(sketch, "E242.0.0", {"start": v(12.75, -7.18) * mm, "mid": v(13.68, -7.04) * mm, "end": v(14.63, -7) * mm});
            skLineSegment(sketch, "E242.0.1", {"start": v(14.63, -7) * mm, "end": v(19, -7) * mm});
            skLineSegment(sketch, "E242.0.2", {"start": v(19, -7) * mm, "end": v(19, -2.9) * mm});
            skLineSegment(sketch, "E242.0.3", {"start": v(19, -2.9) * mm, "end": v(19, -2.5) * mm});
            skArc(sketch, "E242.0.4", {"start": v(19, -2.5) * mm, "mid": v(18.27, -0.73) * mm, "end": v(16.5, 0) * mm});
            skLineSegment(sketch, "E242.0.5", {"start": v(16.5, 0) * mm, "end": v(14.72, 0) * mm});
            skLineSegment(sketch, "E242.0.6", {"start": v(14.72, 0) * mm, "end": v(13, 0) * mm});
            skLineSegment(sketch, "E242.0.7", {"start": v(13, 0) * mm, "end": v(0, 0) * mm});
            skLineSegment(sketch, "E242.0.9", {"start": v(0, -20.71) * mm, "end": v(6.36, -11.37) * mm});
            skArc(sketch, "E242.0.10", {"start": v(6.36, -11.37) * mm, "mid": v(8.12, -9.4) * mm, "end": v(10.33, -7.97) * mm});
            skArc(sketch, "E242.0.11", {"start": v(10.33, -7.97) * mm, "mid": v(11.52, -7.5) * mm, "end": v(12.75, -7.18) * mm});
            skLineSegment(sketch, "E243.0.0", {"start": v(-25.8, -10.45) * mm, "end": v(-33.83, -46.4) * mm});
            skArc(sketch, "E243.0.1", {"start": v(-33.83, -46.4) * mm, "mid": v(-33.96, -47.16) * mm, "end": v(-34, -47.93) * mm});
            skLineSegment(sketch, "E243.0.2", {"start": v(-34, -47.93) * mm, "end": v(-34, -47.93) * mm});
            skArc(sketch, "E243.0.3", {"start": v(-31.75, -47.93) * mm, "mid": v(-30.36, -44.57) * mm, "end": v(-27, -43.18) * mm});
            skArc(sketch, "E243.0.4", {"start": v(-27, -43.18) * mm, "mid": v(-23.64, -44.57) * mm, "end": v(-22.25, -47.93) * mm});
            skLineSegment(sketch, "E243.0.6", {"start": v(-18.53, -47.93) * mm, "end": v(-0.48, -21.42) * mm});
            skLineSegment(sketch, "E243.0.7", {"start": v(-0.48, -21.42) * mm, "end": v(0, -20.71) * mm});
            skLineSegment(sketch, "E243.0.9", {"start": v(0, 0) * mm, "end": v(-13, 0) * mm});
            skLineSegment(sketch, "E243.0.10", {"start": v(-13, 0) * mm, "end": v(-14.72, 0) * mm});
            skLineSegment(sketch, "E243.0.11", {"start": v(-14.72, 0) * mm, "end": v(-16.5, 0) * mm});
            skArc(sketch, "E243.0.12", {"start": v(-16.5, 0) * mm, "mid": v(-18.16, -0.63) * mm, "end": v(-18.98, -2.2) * mm});
            skArc(sketch, "E243.0.13", {"start": v(-18.98, -2.2) * mm, "mid": v(-19.28, -2.8) * mm, "end": v(-19.89, -3.08) * mm});
            skLineSegment(sketch, "E243.0.14", {"start": v(-19.89, -3.08) * mm, "end": v(-24.23, -3.46) * mm});
            skLineSegment(sketch, "E243.0.16", {"start": v(-24.69, -5.5) * mm, "end": v(-25.8, -10.45) * mm});
            skArc(sketch, "E244.0.0", {"start": v(-33.75, -46.04) * mm, "mid": v(-30.35, -54.02) * mm, "end": v(-21.8, -52.56) * mm});
            skLineSegment(sketch, "E245.0.1", {"start": v(-24.23, -3.46) * mm, "end": v(-27, -3.7) * mm});
            skLineSegment(sketch, "E245.0.2", {"start": v(-27, -3.7) * mm, "end": v(-26.83, -5.7) * mm});
            skLineSegment(sketch, "E245.0.3", {"start": v(-26.83, -5.7) * mm, "end": v(-24.69, -5.5) * mm});
            skLineSegment(sketch, "E246.0", {"start": v(6.36, -11.37) * mm, "end": v(-21.21, -51.87) * mm});
            skCircle(sketch, "E247.0", {"center": v(-27, -47.93) * mm, "radius": 4.75 * mm});
            skArc(sketch, "E248", {"start": v(-21.8, -52.56) * mm, "mid": v(-21.47, -52.19) * mm, "end": v(-21.16, -51.8) * mm});
            skSolve(sketch);
        }
        {
            var Q0;
            Q0 = qSketchRegion(id + "F18", true);
            extrude(context, id + "F19", {"entities" : qUnion([Q0]), "endBound" : BoundingType.SYMMETRIC, "depth" : 39 * mm});
        }
        {
            var Q0;
            Q0=qCreatedBy(makeId("Front.planeOp"),FACE);
            var sketch = newSketch(context, id + "F20", { "sketchPlane" : qUnion([Q0])});
            skLineSegment(sketch, "E249.0", {"start": v(-27, -88.43) * mm, "end": v(-27, -40.18) * mm, "construction": true});
            skLineSegment(sketch, "E250.0", {"start": v(-67.5, -47.93) * mm, "end": v(13.5, -47.93) * mm, "construction": true});
            skCircle(sketch, "E251", {"center": v(-27, -47.93) * mm, "radius": 42.5 * mm});
            skSolve(sketch);
        }
        {
            var Q0;
            Q0 = qSketchRegion(id + "F20", true);
            extrude(context, id + "F21", {"entities" : qUnion([Q0]), "operationType" : NewBodyOperationType.REMOVE, "endBound" : BoundingType.SYMMETRIC, "oppositeDirection" : true, "depth" : 26 * mm});
        }
        {
            var Q0;
            Q0=qCreatedBy(makeId("Top.planeOp"),FACE);
            var sketch = newSketch(context, id + "F22", { "sketchPlane" : qUnion([Q0])});
            skArc(sketch, "E252.0", {"start": v(-24.23, 15) * mm, "mid": v(-27, 0) * mm, "end": v(-24.23, -15) * mm});
            skLineSegment(sketch, "E253.0", {"start": v(-13.27, 15) * mm, "end": v(-24.23, 15) * mm});
            skArc(sketch, "E254.0", {"start": v(-13.27, 15) * mm, "mid": v(-11.82, 15.21) * mm, "end": v(-10.5, 15.83) * mm});
            skArc(sketch, "E255.0", {"start": v(-10.5, -15.83) * mm, "mid": v(19, 0) * mm, "end": v(-10.5, 15.83) * mm});
            skArc(sketch, "E256.0", {"start": v(-10.5, -15.83) * mm, "mid": v(-11.82, -15.21) * mm, "end": v(-13.27, -15) * mm});
            skLineSegment(sketch, "E257.0", {"start": v(-13.27, -15) * mm, "end": v(-24.23, -15) * mm});
            skLineSegment(sketch, "E258.0", {"start": v(-19.89, -19.5) * mm, "end": v(-27, -19.5) * mm});
            skLineSegment(sketch, "E259.0", {"start": v(16.5, -19.5) * mm, "end": v(-16.5, -19.5) * mm});
            skLineSegment(sketch, "E260.0.0", {"start": v(16.5, 19.5) * mm, "end": v(-16.5, 19.5) * mm});
            skLineSegment(sketch, "E260.0.1", {"start": v(-16.5, 19.5) * mm, "end": v(-16.5, -19.5) * mm});
            skLineSegment(sketch, "E260.0.2", {"start": v(-16.5, -19.5) * mm, "end": v(16.5, -19.5) * mm});
            skPoint(sketch, "E261.0", {"position": v(18.27, -19.5) * mm});
            skLineSegment(sketch, "E262.0", {"start": v(19, -19.5) * mm, "end": v(19, 19.5) * mm});
            skLineSegment(sketch, "E263.0", {"start": v(19, 19.5) * mm, "end": v(16.5, 19.5) * mm});
            skLineSegment(sketch, "E264.0", {"start": v(-24.69, 19.5) * mm, "end": v(-33.75, 19.5) * mm});
            skLineSegment(sketch, "E265.0", {"start": v(-33.98, 15) * mm, "end": v(-33.98, 19.5) * mm});
            skLineSegment(sketch, "E266", {"start": v(-33.98, 15) * mm, "end": v(-40.75, 15) * mm});
            skLineSegment(sketch, "E267", {"start": v(-40.75, 15) * mm, "end": v(-40.75, -15) * mm});
            skLineSegment(sketch, "E268", {"start": v(-40.75, -15) * mm, "end": v(-34, -15) * mm});
            skLineSegment(sketch, "E269.0", {"start": v(19, -19.5) * mm, "end": v(16.5, -19.5) * mm});
            skLineSegment(sketch, "E270.0", {"start": v(-16.5, -19.5) * mm, "end": v(-18.98, -19.5) * mm});
            skLineSegment(sketch, "E271.0", {"start": v(-18.98, -19.5) * mm, "end": v(-19.89, -19.5) * mm});
            skLineSegment(sketch, "E272.0", {"start": v(-24.69, -19.5) * mm, "end": v(-33.75, -19.5) * mm});
            skLineSegment(sketch, "E273.0", {"start": v(-33.75, -19.5) * mm, "end": v(-33.98, -19.5) * mm});
            skLineSegment(sketch, "E274.0", {"start": v(-34, -19.5) * mm, "end": v(-34, -15) * mm});
            skLineSegment(sketch, "E275.0", {"start": v(-33.75, 19.5) * mm, "end": v(-33.98, 19.5) * mm});
            skLineSegment(sketch, "E276.0", {"start": v(-16.5, 19.5) * mm, "end": v(-18.98, 19.5) * mm});
            skLineSegment(sketch, "E277.0", {"start": v(-18.98, 19.5) * mm, "end": v(-19.89, 19.5) * mm});
            skLineSegment(sketch, "E278.0", {"start": v(-19.89, 19.5) * mm, "end": v(-27, 19.5) * mm});
            skLineSegment(sketch, "E279.0", {"start": v(-34, 15) * mm, "end": v(-34, 19.5) * mm});
            skPoint(sketch, "E280.orphan", {"position": v(-33.5, 15) * mm});
            skPoint(sketch, "E281.orphan", {"position": v(-33.98, 13) * mm});
            skPoint(sketch, "E282.orphan", {"position": v(-34, 13) * mm});
            skPoint(sketch, "E283.orphan", {"position": v(-34, -13) * mm});
            skPoint(sketch, "E284.orphan", {"position": v(-33.5, -15) * mm});
            skSolve(sketch);
        }
        {
            var Q0;
            {var subQ3=sQuery(id+"F22.wireOp",EDGE,"E254.0");Q0=makeQuery(id+"F22.imprint","IMPRINT",FACE,{"disambiguationData":[TD([[makeQuery(id+"F22.imprint","IMPRINT",EDGE,{"derivedFrom":subQ3}),1.0]])]});}
            var Q1;
            {var subQ4=sQuery(id+"F22.wireOp",EDGE,"E256.0");Q1=makeQuery(id+"F22.imprint","IMPRINT",FACE,{"disambiguationData":[TD([[makeQuery(id+"F22.imprint","IMPRINT",EDGE,{"derivedFrom":subQ4}),1.0]])]});}
            extrude(context, id + "F23", {"entities" : qUnion([Q0, Q1]), "operationType" : NewBodyOperationType.REMOVE, "oppositeDirection" : true, "depth" : 71.4 * mm});
        }
        {
            var Q0;
            Q0=qCreatedBy(id+"F7.planeOp",FACE);
            var sketch = newSketch(context, id + "F24", { "sketchPlane" : qUnion([Q0])});
            skArc(sketch, "E285.0", {"start": v(18.99, -25.96) * mm, "mid": v(17.81, -34.98) * mm, "end": v(15.04, -43.63) * mm});
            skLineSegment(sketch, "E286.0", {"start": v(18.99, -25.96) * mm, "end": v(18.99, -2.45) * mm});
            skPoint(sketch, "E287.0", {"position": v(18.25, -0.68) * mm});
            skArc(sketch, "E288.0", {"start": v(17, 0) * mm, "mid": v(18.43, -0.87) * mm, "end": v(18.99, -2.45) * mm});
            skLineSegment(sketch, "E289.0", {"start": v(16.5, 0.05) * mm, "end": v(16.49, 0.05) * mm});
            skArc(sketch, "E290.0", {"start": v(-19.01, -2.45) * mm, "mid": v(-18.46, -0.87) * mm, "end": v(-17.03, 0) * mm});
            skLineSegment(sketch, "E291.0", {"start": v(-19.01, -25.96) * mm, "end": v(-19.01, -2.45) * mm});
            skArc(sketch, "E292.0", {"start": v(-15.28, -43.13) * mm, "mid": v(-17.9, -34.71) * mm, "end": v(-19.01, -25.96) * mm});
            skLineSegment(sketch, "E293.0", {"start": v(-15.01, -54.88) * mm, "end": v(-15.01, -43.33) * mm});
            skLineSegment(sketch, "E294.0", {"start": v(14.99, -54.88) * mm, "end": v(14.99, -43.63) * mm});
            skLineSegment(sketch, "E295", {"start": v(19.5, -54.88) * mm, "end": v(14.99, -54.88) * mm});
            skLineSegment(sketch, "E296.0", {"start": v(19.5, -47.93) * mm, "end": v(19.5, -54.88) * mm});
            skPoint(sketch, "E297.0", {"position": v(19.24, -47.88) * mm});
            skPoint(sketch, "E298.0", {"position": v(19.5, -47.39) * mm});
            skLineSegment(sketch, "E299.0", {"start": v(19.5, -5.5) * mm, "end": v(19.5, -46.04) * mm});
            skPoint(sketch, "E300.0", {"position": v(19.5, -47.66) * mm});
            skLineSegment(sketch, "E301.0", {"start": v(19.5, -47.39) * mm, "end": v(19.5, -47.93) * mm});
            skLineSegment(sketch, "E302.0", {"start": v(19.5, -46.04) * mm, "end": v(19.5, -47.39) * mm});
            skLineSegment(sketch, "E303.0", {"start": v(19.5, -3.7) * mm, "end": v(19.5, -5.7) * mm});
            skLineSegment(sketch, "E304.0", {"start": v(19.5, -3.08) * mm, "end": v(19.5, -3.7) * mm});
            skPoint(sketch, "E305.0", {"position": v(19.5, -2.8) * mm});
            skLineSegment(sketch, "E306.0", {"start": v(19.5, -2.2) * mm, "end": v(19.5, -3.08) * mm});
            skLineSegment(sketch, "E307.0", {"start": v(19.5, 0) * mm, "end": v(19.5, -2.2) * mm});
            skLineSegment(sketch, "E308.0", {"start": v(19.5, 0) * mm, "end": v(17, 0) * mm});
            skLineSegment(sketch, "E309.0", {"start": v(-19.5, 0) * mm, "end": v(-17.03, 0) * mm});
            skLineSegment(sketch, "E310.0", {"start": v(-19.5, 0) * mm, "end": v(-19.5, -2.2) * mm});
            skLineSegment(sketch, "E311.0", {"start": v(-19.5, -2.2) * mm, "end": v(-19.5, -3.08) * mm});
            skLineSegment(sketch, "E312.0", {"start": v(-19.5, -3.08) * mm, "end": v(-19.5, -3.7) * mm});
            skLineSegment(sketch, "E313.0", {"start": v(-19.5, -3.7) * mm, "end": v(-19.5, -5.7) * mm});
            skLineSegment(sketch, "E314.0", {"start": v(-19.5, -5.5) * mm, "end": v(-19.5, -46.04) * mm});
            skLineSegment(sketch, "E315", {"start": v(-15.01, -54.88) * mm, "end": v(-19.5, -54.88) * mm});
            skArc(sketch, "E316.0", {"start": v(-15.22, -43.13) * mm, "mid": v(-15.08, -43.19) * mm, "end": v(-15.01, -43.33) * mm});
            skLineSegment(sketch, "E317.0", {"start": v(-15.28, -43.13) * mm, "end": v(-15.21, -43.13) * mm});
            skPoint(sketch, "E318.orphan", {"position": v(-16.01, -43.13) * mm});
            skPoint(sketch, "E319.orphan", {"position": v(-15.01, -6.65) * mm});
            skPoint(sketch, "E320.orphan", {"position": v(-16.51, 0.05) * mm});
            skPoint(sketch, "E321.orphan", {"position": v(-15, 0) * mm});
            skPoint(sketch, "E322.orphan", {"position": v(15, 0) * mm});
            skArc(sketch, "E323.0", {"start": v(14.99, -43.63) * mm, "mid": v(15.01, -43.63) * mm, "end": v(15.04, -43.63) * mm});
            skPoint(sketch, "E324.orphan", {"position": v(16.49, -45.13) * mm});
            skPoint(sketch, "E325.orphan", {"position": v(14.99, -6.65) * mm});
            skLineSegment(sketch, "E326.0", {"start": v(-19.5, -47.93) * mm, "end": v(-19.5, -54.88) * mm});
            skLineSegment(sketch, "E327.0", {"start": v(-19.5, -47.39) * mm, "end": v(-19.5, -47.93) * mm});
            skLineSegment(sketch, "E328.0", {"start": v(-19.5, -46.04) * mm, "end": v(-19.5, -47.39) * mm});
            skSolve(sketch);
        }
        {
            var Q0;
            Q0 = qSketchRegion(id + "F24", true);
            extrude(context, id + "F25", {"entities" : qUnion([Q0]), "operationType" : NewBodyOperationType.REMOVE, "endBound" : BoundingType.SYMMETRIC, "depth" : 113.2 * mm});
        }
    });
